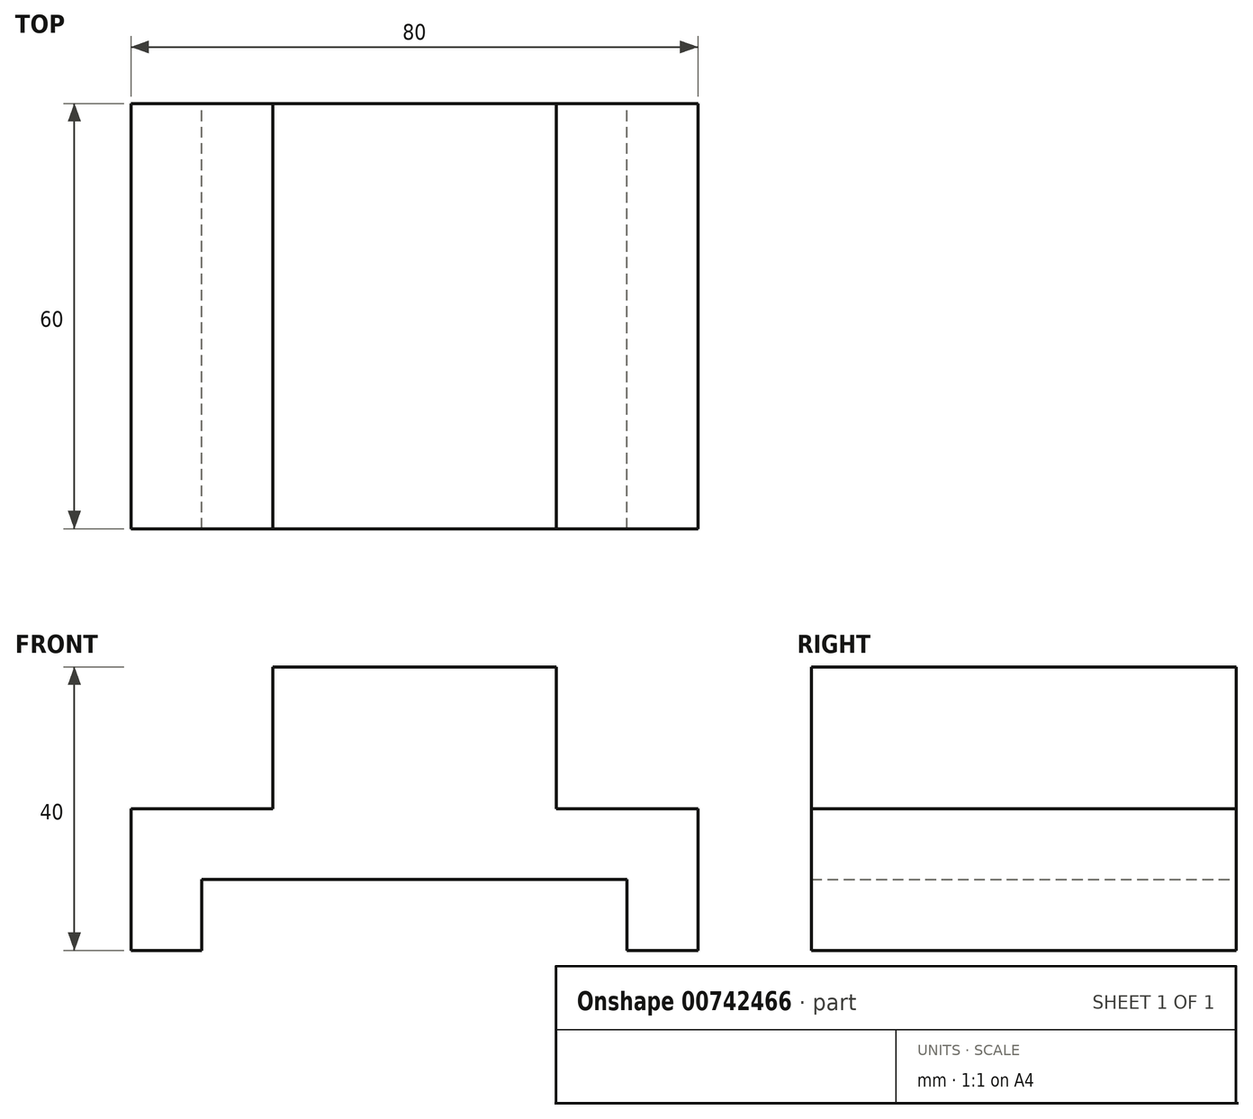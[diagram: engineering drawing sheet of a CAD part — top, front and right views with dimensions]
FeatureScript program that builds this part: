
annotation { "Feature Type Name" : "Feature", "Feature Type Description" : "" }
export const myFeature = defineFeature(function(context is Context, id is Id, definition is map)
    precondition{}
    {
        {
            var Q0;
            Q0=qCreatedBy(makeId("Front.planeOp"),FACE);
            var sketch = newSketch(context, id + "F0", { "sketchPlane" : qUnion([Q0])});
            skLineSegment(sketch, "E0", {"start": v(0, 0) * mm, "end": v(0, 20) * mm});
            skLineSegment(sketch, "E1", {"start": v(0, 20) * mm, "end": v(20, 20) * mm});
            skLineSegment(sketch, "E2", {"start": v(20, 20) * mm, "end": v(20, 40) * mm});
            skLineSegment(sketch, "E3", {"start": v(20, 40) * mm, "end": v(60, 40) * mm});
            skLineSegment(sketch, "E4", {"start": v(60, 40) * mm, "end": v(60, 20) * mm});
            skLineSegment(sketch, "E5", {"start": v(60, 20) * mm, "end": v(80, 20) * mm});
            skLineSegment(sketch, "E6", {"start": v(80, 20) * mm, "end": v(80, 0) * mm});
            skLineSegment(sketch, "E7", {"start": v(80, 0) * mm, "end": v(70, 0) * mm});
            skLineSegment(sketch, "E8", {"start": v(70, 0) * mm, "end": v(70, 10) * mm});
            skLineSegment(sketch, "E9", {"start": v(70, 10) * mm, "end": v(10, 10) * mm});
            skLineSegment(sketch, "E10", {"start": v(10, 10) * mm, "end": v(10, 0) * mm});
            skLineSegment(sketch, "E11", {"start": v(10, 0) * mm, "end": v(0, 0) * mm});
            skSolve(sketch);
        }
        {
            var Q0;
            Q0 = qSketchRegion(id + "F0", true);
            extrude(context, id + "F1", {"entities" : qUnion([Q0]), "depth" : 60 * mm, "offsetDistance" : 25 * mm});
        }
    });
